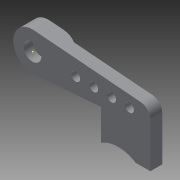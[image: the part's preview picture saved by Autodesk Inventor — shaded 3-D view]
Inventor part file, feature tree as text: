
AUTODESK INVENTOR PART (.ipt)
format: ipt  version: 2015 SP2 (Build 190223200, 223)  size: 171,520 bytes
history: native  units: mm
features: sketch x12, extrude x7, hole x3, fillet x1
ambient origin geometry x8: Origin, YZ Plane, XZ Plane, XY Plane, X Axis, Y Axis, Z Axis, Center Point
bodies: Solid1 (feature_tree)
feature tree (23):
  extrude  "Extrusion1"  Depth=11.314mm
  extrude  "Extrusion2"  Depth=36.0mm
  fillet  "Fillet1"  Radius=7.0mm
  extrude  "Extrusion3"  Depth=4.0mm
  sketch  "Sketch4"  dims[d8=1.5mm d9=0.0mm d10=10.0mm]
  extrude  "Extrusion4"  Depth=10.0mm
  sketch  "Sketch6"  dims[d14=5.8mm d15=5.9mm]
  hole  "Hole1"  [1 undecoded]
  sketch  "Sketch7"  dims[d16=3.0mm d17=0.0mm d18=2.7mm]
  hole  "Hole2"  [1 undecoded]
  extrude  "Extrusion5"  Depth=2.7mm
  extrude  "Extrusion6"  Depth=4.0mm
  hole  "Hole3"  [1 undecoded]
  extrude  "Extrusion7"  Depth=3.0mm
  sketch  "Sketch1"  dims[d0=12.9mm d1=11.314mm]
  sketch  "Sketch2"  dims[d2=5.7mm d3=36.0mm d4=7.0mm]
  sketch  "Sketch3"  dims[d5=4.0mm d6=0.0mm d7=12.9mm]
  sketch  "Sketch5"  dims[d11=11.314mm d12=1.5mm d13=0.0mm]
  sketch  "Sketch8"  dims[d19=2.7mm d20=6.0mm d21=4.0mm d22=2.0mm d23=90.0deg d24=8.0mm d25=20.594885mm d27=6.0mm]
  sketch  "Sketch9"  dims[d28=3.0mm d29=6.0mm]
  sketch  "Sketch10"  dims[d30=3.0mm d31=3.0mm]
  sketch  "Sketch11"  dims[d32=3.0mm]
  sketch  "Sketch12"  dims[d33=3.0mm d34=3.0mm d35=3.0mm d36=6.0mm d37=4.0mm d38=2.0mm d39=90.0deg d40=8.0mm d41=20.594885mm d42=4.0mm d43=0.0mm d44=4.0mm d45=0.0mm d46=15.0mm d47=3.0mm d48=3.0mm d49=3.0mm d50=6.0mm d51=4.0mm d52=2.0mm d53=90.0deg d54=8.0mm d55=20.594885mm d56=4.0mm d57=0.0mm]
note: 3 required parameter values undecoded (feature->parameter linkage not recoverable at this tier; creation-order binding heuristic only, values carry confidence <= 0.55)
